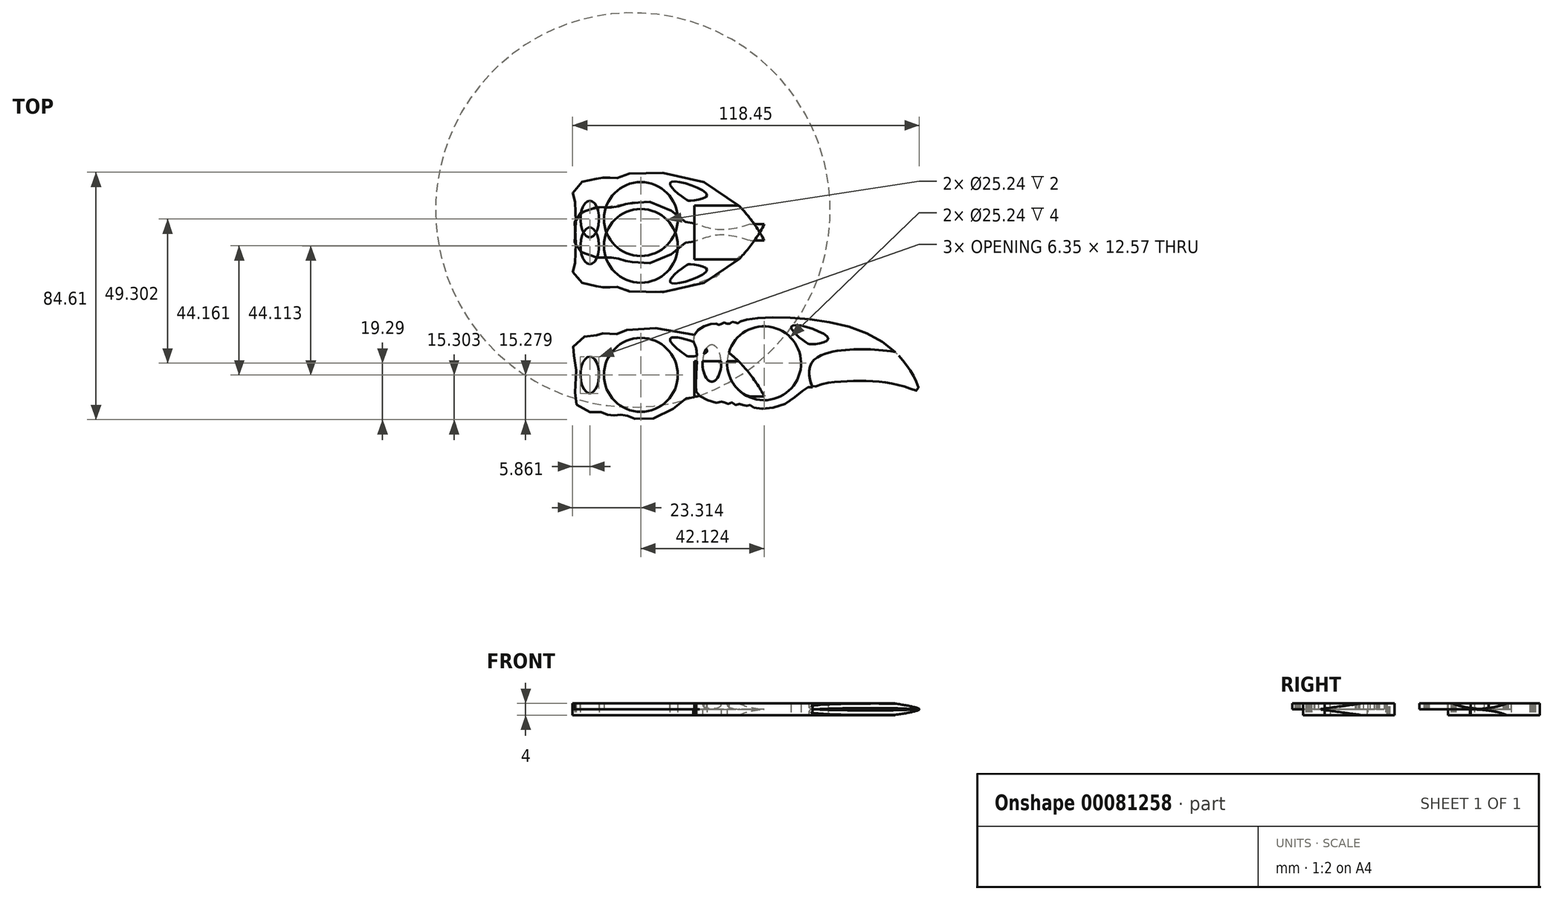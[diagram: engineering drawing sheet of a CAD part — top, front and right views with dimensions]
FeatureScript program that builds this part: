
annotation { "Feature Type Name" : "Feature", "Feature Type Description" : "" }
export const myFeature = defineFeature(function(context is Context, id is Id, definition is map)
    precondition{}
    {
        {
            var Q0;
            Q0=qCreatedBy(makeId("Top.planeOp"),FACE);
            var sketch = newSketch(context, id + "F0", { "sketchPlane" : qUnion([Q0])});
            skEllipse(sketch, "E0", {"center": v(-65.76, 31.2) * mm, "majorRadius": 3.18 * mm, "minorRadius": 6.28 * mm, "majorAxis": v(1, 0)});
            skSolve(sketch);
        }
        {
            var Q0;
            Q0=qCreatedBy(makeId("Top.planeOp"),FACE);
            var sketch = newSketch(context, id + "F1", { "sketchPlane" : qUnion([Q0])});
            skFitSpline(sketch, "E1", {"points": [v(-36.66, 44.1) * mm, v(-25.65, 39.46) * mm, v(-31, 37.53) * mm, v(-33.18, 38.12) * mm, v(-38.3, 43) * mm, v(-36.66, 44.1) * mm]});
            skSolve(sketch);
        }
        {
            var Q0;
            Q0=qCreatedBy(makeId("Top.planeOp"),FACE);
            var sketch = newSketch(context, id + "F2", { "sketchPlane" : qUnion([Q0])});
            skFitSpline(sketch, "E2", {"points": [v(-5.8, 22.79) * mm, v(-22.84, 42) * mm, v(-55.15, 46.02) * mm, v(-56.65, 45.22) * mm, v(-58.15, 45.72) * mm, v(-59.65, 44.92) * mm, v(-61.15, 45.42) * mm, v(-62.65, 44.62) * mm, v(-64.15, 45.12) * mm, v(-70.58, 42.3) * mm, v(-71.52, 38.88) * mm, v(-70.6, 36.15) * mm, v(-70.85, 23.65) * mm, v(-69.7, 20.57) * mm, v(-63.04, 18.04) * mm, v(-61.54, 18.54) * mm, v(-60.04, 17.64) * mm, v(-58.54, 18.14) * mm, v(-57.04, 17.24) * mm, v(-55.54, 17.74) * mm, v(-54.04, 16.84) * mm, v(-52.54, 17.34) * mm, v(-51.04, 16.44) * mm, v(-40.36, 17.68) * mm, v(-32.62, 23.3) * mm, v(-30.94, 23.36) * mm, v(-22.2, 25.7) * mm, v(-10.29, 23.64) * mm, v(-7, 22.68) * mm, v(-5.93, 22.49) * mm, v(-5.8, 22.79) * mm]});
            skSolve(sketch);
        }
        {
            var Q0;
            Q0=qCreatedBy(makeId("Top.planeOp"),FACE);
            var sketch = newSketch(context, id + "F3", { "sketchPlane" : qUnion([Q0])});
            skCircle(sketch, "E3", {"center": v(-48.3, 31.23) * mm, "radius": 12.62 * mm});
            skSolve(sketch);
        }
        {
            var Q0;
            Q0 = qSketchRegion(id + "F2", true);
            extrude(context, id + "F4", {"entities" : qUnion([Q0]), "depth" : 2 * mm, "hasSecondDirection" : true, "secondDirectionOppositeDirection" : true, "secondDirectionDepth" : 2 * mm});
        }
        {
            var Q0;
            Q0 = qSketchRegion(id + "F3", true);
            extrude(context, id + "F5", {"entities" : qUnion([Q0]), "operationType" : NewBodyOperationType.REMOVE, "depth" : 5 * mm, "hasSecondDirection" : true, "secondDirectionOppositeDirection" : true, "secondDirectionDepth" : 2 * mm});
        }
        {
            var Q0;
            Q0 = qSketchRegion(id + "F1", true);
            extrude(context, id + "F6", {"entities" : qUnion([Q0]), "operationType" : NewBodyOperationType.REMOVE, "oppositeDirection" : true, "depth" : 25 * mm, "hasSecondDirection" : true, "secondDirectionOppositeDirection" : false, "secondDirectionDepth" : 25 * mm});
        }
        {
            var Q0;
            Q0 = qSketchRegion(id + "F0", true);
            extrude(context, id + "F7", {"entities" : qUnion([Q0]), "operationType" : NewBodyOperationType.REMOVE, "depth" : 25 * mm, "hasSecondDirection" : true, "secondDirectionOppositeDirection" : true, "secondDirectionDepth" : 25 * mm});
        }
        {
            var Q0;
            Q0=qCreatedBy(makeId("Right.planeOp"),FACE);
            var sketch = newSketch(context, id + "F8", { "sketchPlane" : qUnion([Q0])});
            skFitSpline(sketch, "E4.MirrorC", {"points": [v(14.7, 0) * mm, v(35.57, -1.87) * mm, v(42.87, -10.54) * mm, v(39.47, -18.44) * mm, v(31.48, -19.05) * mm, v(8, -4.72) * mm, v(6.87, -0.5) * mm, v(7.8, 0.06) * mm, v(14.7, 0) * mm]});
            skFitSpline(sketch, "E5.MirrorC", {"points": [v(14.7, 0) * mm, v(35.57, 1.87) * mm, v(42.87, 10.54) * mm, v(39.47, 18.44) * mm, v(31.48, 19.05) * mm, v(8, 4.72) * mm, v(6.87, 0.5) * mm, v(7.8, -0.06) * mm, v(14.7, 0) * mm]});
            skSolve(sketch);
        }
        {
            var Q0;
            Q0 = qSketchRegion(id + "F8", true);
            extrude(context, id + "F9", {"entities" : qUnion([Q0]), "operationType" : NewBodyOperationType.REMOVE, "oppositeDirection" : true, "depth" : 30 * mm});
        }
        {
            var Q0;
            Q0=makeQuery(id+"F4.opExtrude","SWEPT_BODY",BODY,{"disambiguationData":[OSD([sQuery(id+"F2.wireOp",EDGE,"E2")])]});
            transform(context, id + "F10", {"entities" : qUnion([Q0]), "transformType" : TransformType.TRANSLATION_3D, "dx" : 0 * mm, "dy" : -53.3 * mm, "dz" : 0 * mm, "makeCopy" : true});
        }
        {
            var Q0;
            Q0=qCreatedBy(makeId("Top.planeOp"),FACE);
            var sketch = newSketch(context, id + "F11", { "sketchPlane" : qUnion([Q0])});
            skLineSegment(sketch, "E6.bottom", {"start": v(-74.32, -0.57) * mm, "end": v(-3.4, -0.57) * mm});
            skLineSegment(sketch, "E6.top", {"start": v(-74.32, -43.07) * mm, "end": v(-3.4, -43.07) * mm});
            skLineSegment(sketch, "E6.left", {"start": v(-74.32, -0.57) * mm, "end": v(-74.32, -43.07) * mm});
            skLineSegment(sketch, "E6.right", {"start": v(-3.4, -0.57) * mm, "end": v(-3.4, -43.07) * mm});
            skSolve(sketch);
        }
        {
            var Q0;
            Q0 = qSketchRegion(id + "F11", true);
            extrude(context, id + "F12", {"entities" : qUnion([Q0]), "operationType" : NewBodyOperationType.REMOVE, "oppositeDirection" : true, "depth" : 25 * mm});
        }
        {
            var Q0;
            Q0=makeQuery(id+"F10.opPattern","COPY",BODY,{"derivedFrom":makeQuery(id+"F4.opExtrude","SWEPT_BODY",BODY,{"disambiguationData":[OSD([sQuery(id+"F2.wireOp",EDGE,"E2")])]}),"instanceName":"1"});
            var Q1;
            Q1=qCreatedBy(makeId("Front.planeOp"),FACE);
            mirror(context, id + "F13", {"entities" : qUnion([Q0]), "mirrorPlane" : qUnion([Q1])});
        }
        {
            var Q0;
            Q0=qCreatedBy(makeId("Top.planeOp"),FACE);
            var sketch = newSketch(context, id + "F14", { "sketchPlane" : qUnion([Q0])});
            skFitSpline(sketch, "E7", {"points": [v(46.83, -9.22) * mm, v(32.64, 8.4) * mm, v(-13.86, 14.48) * mm, v(-15.36, 13.68) * mm, v(-16.86, 14.18) * mm, v(-18.36, 13.38) * mm, v(-19.86, 13.88) * mm, v(-21.36, 13.08) * mm, v(-22.86, 13.58) * mm, v(-29.3, 10.76) * mm, v(-30.23, 7.34) * mm, v(-29.31, 4.6) * mm, v(-29.56, -7.88) * mm, v(-28.4, -10.97) * mm, v(-21.75, -13.5) * mm, v(-20.25, -13) * mm, v(-18.75, -13.9) * mm, v(-17.25, -13.4) * mm, v(-15.75, -14.3) * mm, v(-14.25, -13.8) * mm, v(-12.75, -14.7) * mm, v(-11.25, -14.2) * mm, v(-9.75, -15.1) * mm, v(0.93, -13.86) * mm, v(8.67, -8.24) * mm, v(10.35, -8.17) * mm, v(13.87, -7.06) * mm, v(36.4, -6.75) * mm, v(45.64, -9.32) * mm, v(46.7, -9.51) * mm, v(46.83, -9.22) * mm]});
            skSolve(sketch);
        }
        {
            var Q0;
            Q0=qCreatedBy(makeId("Top.planeOp"),FACE);
            var sketch = newSketch(context, id + "F15", { "sketchPlane" : qUnion([Q0])});
            skEllipse(sketch, "E8", {"center": v(-24.04, 0) * mm, "majorRadius": 3.18 * mm, "minorRadius": 6.28 * mm, "majorAxis": v(1, 0)});
            skSolve(sketch);
        }
        {
            var Q0;
            Q0=qCreatedBy(makeId("Top.planeOp"),FACE);
            var sketch = newSketch(context, id + "F16", { "sketchPlane" : qUnion([Q0])});
            skFitSpline(sketch, "E9", {"points": [v(4.75, 13.05) * mm, v(15.75, 8.41) * mm, v(10.4, 6.5) * mm, v(8.22, 7.08) * mm, v(3.11, 11.95) * mm, v(4.75, 13.05) * mm]});
            skSolve(sketch);
        }
        {
            var Q0;
            Q0=qCreatedBy(makeId("Top.planeOp"),FACE);
            var sketch = newSketch(context, id + "F17", { "sketchPlane" : qUnion([Q0])});
            skCircle(sketch, "E10", {"center": v(-6.18, 0) * mm, "radius": 12.62 * mm});
            skSolve(sketch);
        }
        {
            var Q0;
            Q0 = qSketchRegion(id + "F14", true);
            extrude(context, id + "F18", {"entities" : qUnion([Q0]), "depth" : 2 * mm});
        }
        {
            var Q0;
            Q0 = qSketchRegion(id + "F15", true);
            extrude(context, id + "F19", {"entities" : qUnion([Q0]), "operationType" : NewBodyOperationType.REMOVE, "depth" : 25 * mm, "hasSecondDirection" : true, "secondDirectionOppositeDirection" : true, "secondDirectionDepth" : 25 * mm});
        }
        {
            var Q0;
            Q0 = qSketchRegion(id + "F16", true);
            extrude(context, id + "F20", {"entities" : qUnion([Q0]), "operationType" : NewBodyOperationType.REMOVE, "depth" : 25 * mm, "hasSecondDirection" : true, "secondDirectionOppositeDirection" : true, "secondDirectionDepth" : 25 * mm});
        }
        {
            var Q0;
            Q0 = qSketchRegion(id + "F17", true);
            extrude(context, id + "F21", {"entities" : qUnion([Q0]), "operationType" : NewBodyOperationType.REMOVE, "depth" : 25 * mm, "hasSecondDirection" : true, "secondDirectionOppositeDirection" : true, "secondDirectionDepth" : 25 * mm});
        }
        {
            var Q0;
            Q0=qCreatedBy(makeId("Right.planeOp"),FACE);
            var sketch = newSketch(context, id + "F22", { "sketchPlane" : qUnion([Q0])});
            skLineSegment(sketch, "E11", {"start": v(-7.17, 0) * mm, "end": v(6.77, 1.98) * mm});
            skSolve(sketch);
        }
        {
            var Q0;
            Q0=sQuery(id+"F22.wireOp",EDGE,"E11");
            cPlane(context, id + "F23", {"entities" : qUnion([Q0]), "cplaneType" : CPlaneType.LINE_ANGLE, "offset" : 150 * mm, "angle" : 359.5 * degree, "width" : 150 * mm, "height" : 150 * mm});
        }
        {
            var Q0;
            Q0=qCreatedBy(id+"F23.planeOp",FACE);
            var sketch = newSketch(context, id + "F24", { "sketchPlane" : qUnion([Q0])});
            skFitSpline(sketch, "E12", {"points": [v(11.18, -10.19) * mm, v(10.5, 0.98) * mm, v(45.02, 2.5) * mm, v(49.9, -2.6) * mm, v(52.45, -11.68) * mm, v(48.42, -22.4) * mm, v(46, -22.94) * mm, v(12.93, -15.07) * mm, v(11.59, -12.09) * mm, v(11.18, -10.19) * mm]});
            skSolve(sketch);
        }
        {
            var Q0;
            Q0 = qSketchRegion(id + "F24", true);
            extrude(context, id + "F25", {"entities" : qUnion([Q0]), "operationType" : NewBodyOperationType.REMOVE, "depth" : 25 * mm});
        }
        {
            var Q0;
            Q0=makeQuery(id+"F18.opExtrude","SWEPT_BODY",BODY,{"disambiguationData":[OSD([sQuery(id+"F14.wireOp",EDGE,"E7")])]});
            transform(context, id + "F26", {"entities" : qUnion([Q0]), "transformType" : TransformType.TRANSLATION_3D, "dx" : 0 * mm, "dy" : -18.07 * mm, "dz" : 0 * mm, "makeCopy" : false});
        }
        {
            var Q0;
            Q0=makeQuery(id+"F18.opExtrude","SWEPT_BODY",BODY,{"disambiguationData":[OSD([sQuery(id+"F14.wireOp",EDGE,"E7")])]});
            var Q1;
            Q1=qCreatedBy(makeId("Top.planeOp"),FACE);
            mirror(context, id + "F27", {"operationType" : NewBodyOperationType.ADD, "entities" : qUnion([Q0]), "mirrorPlane" : qUnion([Q1])});
        }
    });
